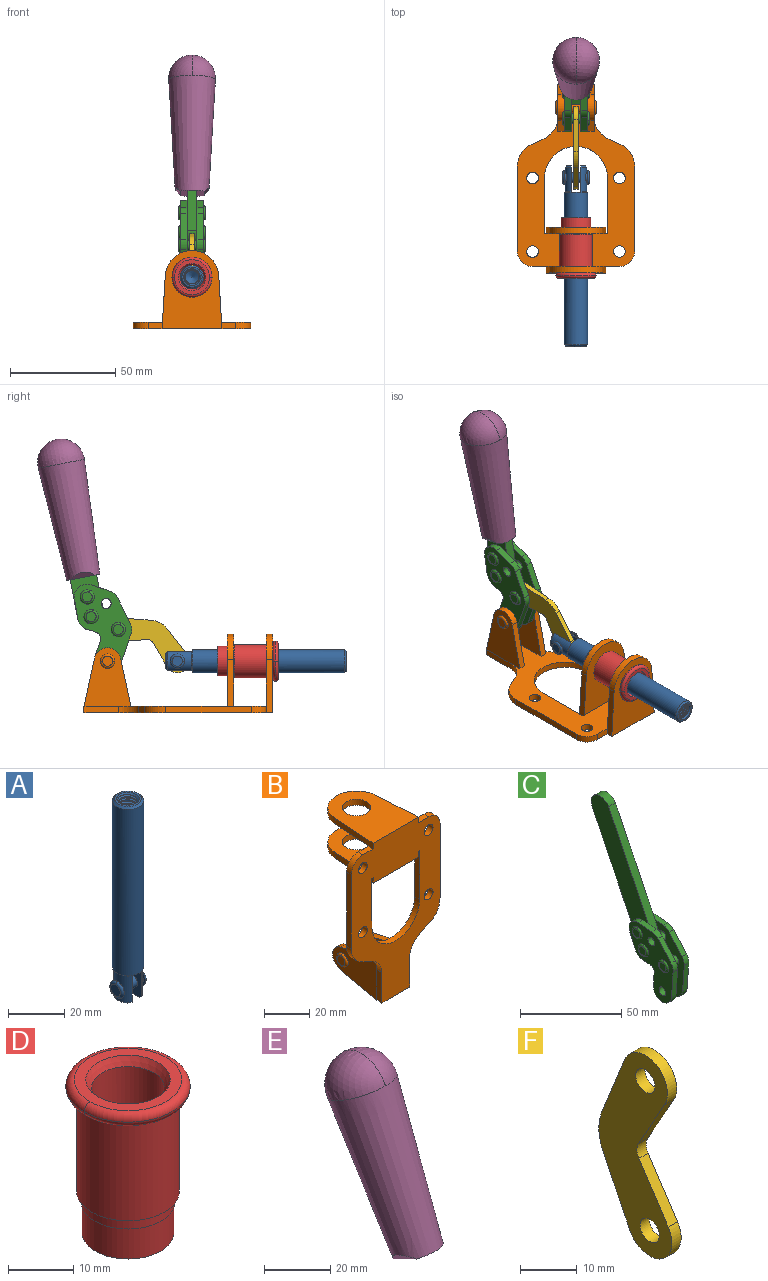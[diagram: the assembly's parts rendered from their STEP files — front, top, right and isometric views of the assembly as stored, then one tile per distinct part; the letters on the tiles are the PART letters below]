
ASSEMBLY  parts=6 mates=6
PART A: 48 faces, bbox 12.6x11.1x86.1 mm
  f0: torus R=2.41mm, axis (-1,0,0), area 15mm2, adj f30,f32,f34
  f1: torus R=2.41mm, axis (-1,0,0), area 15mm2, adj f29,f31,f33
  f2: cylinder r=5.54mm len=72.39mm, axis (0,0,1), area 2518.5mm2, adj f3,f4,f42,f43
  f3: cone r=5.54mm half-angle=45deg, axis (0,0,1), area 7.6mm2, adj f2,f5,f41
  f4: cone r=5.54mm half-angle=45deg, axis (0,0,-1), area 34.9mm2, adj f2,f39
  f5: cylinder r=5.08mm len=11.48mm, axis (0,0,1), area 108.3mm2, adj f3,f7,f8,f41
  f6: cylinder r=2.41mm len=4.83mm, axis (-1,0,0), area 71.2mm2, adj f40,f41
  f7: cylinder r=2.41mm len=4.83mm, axis (-1,0,0), area 7.6mm2, adj f5,f34
  f8: cone r=5.08mm half-angle=45deg, axis (0,0,1), area 10.6mm2, adj f5,f37,f41
  f9: cone r=3.98mm half-angle=45deg, axis (0,0,1), area 17.6mm2, adj f27,f39,f45,f46,f47
  f10: cylinder r=2.41mm len=4.83mm, axis (-1,0,0), area 7.6mm2, adj f33,f38
  f11: cylinder r=3.2mm len=6.4mm, axis (0,0,1), area 78.4mm2, adj f12,f28,f44,f45,f47
  f12: cylinder r=3.2mm len=6.4mm, axis (0,0,1), area 10.5mm2, adj f11,f13,f45,f47
  f13: cylinder r=3.2mm len=6.4mm, axis (0,0,1), area 10.5mm2, adj f12,f14,f45,f47
  f14: cylinder r=3.2mm len=6.4mm, axis (0,0,1), area 10.5mm2, adj f13,f15,f45,f47
  f15: cylinder r=3.2mm len=6.4mm, axis (0,0,1), area 10.5mm2, adj f14,f16,f45,f47
  f16: cylinder r=3.2mm len=6.4mm, axis (0,0,1), area 10.5mm2, adj f15,f17,f45,f47
  f17: cylinder r=3.2mm len=6.4mm, axis (0,0,1), area 10.5mm2, adj f16,f18,f45,f47
  f18: cylinder r=3.2mm len=6.4mm, axis (0,0,1), area 10.5mm2, adj f17,f19,f45,f47
  f19: cylinder r=3.2mm len=6.4mm, axis (0,0,1), area 10.5mm2, adj f18,f20,f45,f47
  f20: cylinder r=3.2mm len=6.4mm, axis (0,0,1), area 10.5mm2, adj f19,f21,f45,f47
  f21: cylinder r=3.2mm len=6.4mm, axis (0,0,1), area 10.5mm2, adj f20,f22,f45,f47
  f22: cylinder r=3.2mm len=6.4mm, axis (0,0,1), area 10.5mm2, adj f21,f23,f45,f47
  f23: cylinder r=3.2mm len=6.4mm, axis (0,0,1), area 10.5mm2, adj f22,f24,f45,f47
  f24: cylinder r=3.2mm len=6.4mm, axis (0,0,1), area 10.5mm2, adj f23,f25,f45,f47
  f25: cylinder r=3.2mm len=6.4mm, axis (0,0,1), area 10.5mm2, adj f24,f26,f45,f47
  f26: cylinder r=3.2mm len=6.4mm, axis (0,0,1), area 10.5mm2, adj f25,f27,f45,f47
  f27: cylinder r=3.2mm len=6.4mm, axis (0,0,1), area 7.4mm2, adj f9,f26,f45,f47
  f28: cone r=3.2mm half-angle=60deg, axis (0,0,1), area 37.2mm2, adj f11
  f29: plane 4.83x4.83mm, normal (-1,0,0), area 18.3mm2, adj f1,f31
  f30: plane 4.83x4.83mm, normal (1,0,0), area 18.3mm2, adj f0,f32
  f31: torus R=2.41mm, axis (-1,0,0), area 15mm2, adj f1,f29,f33
  f32: torus R=2.41mm, axis (-1,0,0), area 15mm2, adj f0,f30,f34
  f33: plane 6.83x6.83mm, normal (1,0,0), area 18.3mm2, adj f1,f10,f31
  f34: plane 6.83x6.83mm, normal (-1,0,0), area 18.3mm2, adj f0,f7,f32
  f35: cone r=5.08mm half-angle=45deg, axis (0,0,1), area 10.6mm2, adj f36,f38,f40
  f36: plane 7.25x1.97mm, normal (0,0,-1), area 10mm2, adj f35,f40
  f37: plane 7.25x1.97mm, normal (0,0,-1), area 10mm2, adj f8,f41
  f38: cylinder r=5.08mm len=11.48mm, axis (0,0,1), area 108.3mm2, adj f10,f35,f40,f42
  f39: plane 9.55x9.55mm, normal (0,0,1), area 22mm2, adj f4,f9
  f40: plane 12.76x10.09mm, normal (1,0,0), area 95.7mm2, adj f6,f35,f36,f38,f42,f43
  f41: plane 12.76x10.09mm, normal (-1,0,0), area 95.7mm2, adj f3,f5,f6,f8,f37,f43
  f42: cone r=5.54mm half-angle=45deg, axis (0,0,1), area 7.6mm2, adj f2,f38,f40
  f43: plane 11.07x4.7mm, normal (0,0,-1), area 50.4mm2, adj f2,f40,f41
  f44: plane 0.89x0.62mm, normal (-1,0,0), area 0.3mm2, adj f11,f45,f46,f47
  f45: bspline ~24.8x7.63mm, area 266.6mm2, adj f9,f11,f12,f13,f14,f15,f16,f17
  f46: bspline ~24.87x7.63mm, area 73.6mm2, adj f9,f44,f45,f47
  f47: bspline ~24.98x7.63mm, area 272.5mm2, adj f9,f11,f12,f13,f14,f15,f16,f17
PART B: 55 faces, bbox 55.7x37.4x89.8 mm
  f0: torus R=2.41mm, axis (-1,0,0), area 15mm2, adj f11,f15,f25
  f1: torus R=2.41mm, axis (-1,0,0), area 15mm2, adj f10,f12,f22
  f2: cylinder r=2.78mm len=5.56mm, axis (0,-1,0), area 54.2mm2, adj f30,f54
  f3: cylinder r=14.99mm len=29.97mm, axis (0,-1,0), area 145.9mm2, adj f30,f49,f53,f54
  f4: cylinder r=2.78mm len=5.56mm, axis (0,-1,0), area 54.2mm2, adj f30,f54
  f5: cylinder r=2.78mm len=5.56mm, axis (0,-1,0), area 54.2mm2, adj f30,f54
  f6: cylinder r=2.78mm len=5.56mm, axis (0,-1,0), area 54.2mm2, adj f30,f54
  f7: cylinder r=6.35mm len=12.7mm, axis (0,0,1), area 123.6mm2, adj f27,f51
  f8: cylinder r=6.35mm len=12.7mm, axis (0,0,-1), area 124.7mm2, adj f21,f35
  f9: cylinder r=2.41mm len=11.18mm, axis (-1,0,0), area 169.4mm2, adj f16,f19
  f10: plane 4.83x4.83mm, normal (1,0,0), area 18.3mm2, adj f1,f12
  f11: plane 4.83x4.83mm, normal (-1,0,0), area 18.3mm2, adj f0,f15
  f12: torus R=2.41mm, axis (-1,0,0), area 15mm2, adj f1,f10,f22
  f13: cylinder r=6.35mm len=12.41mm, axis (1,0,0), area 53.4mm2, adj f18,f19,f22,f23
  f14: cylinder r=6.35mm len=12.41mm, axis (-1,0,0), area 53.4mm2, adj f16,f17,f24,f25
  f15: torus R=2.41mm, axis (-1,0,0), area 15mm2, adj f0,f11,f25
  f16: plane 27.86x22.35mm, normal (1,0,0), area 425.4mm2, adj f9,f14,f17,f24,f30
  f17: plane 22.86x4.97mm, normal (0,0.21,0.98), area 72.5mm2, adj f14,f16,f25,f30
  f18: plane 22.86x4.97mm, normal (0,0.21,0.98), area 72.5mm2, adj f13,f19,f22,f30
  f19: plane 27.86x22.35mm, normal (-1,0,0), area 425.4mm2, adj f9,f13,f18,f23,f30
  f20: cylinder r=12.7mm len=25.35mm, axis (0,0,-1), area 119.8mm2, adj f21,f34,f35,f36
  f21: plane 34.21x28.07mm, normal (0,0,-1), area 702.4mm2, adj f8,f20,f30,f34,f36
  f22: plane 27.96x22.45mm, normal (1,0,0), area 407.2mm2, adj f1,f12,f13,f18,f23,f30,f42,f43
  f23: plane 22.86x4.97mm, normal (0,0.21,-0.98), area 72.5mm2, adj f13,f19,f22,f44
  f24: plane 22.86x4.97mm, normal (0,0.21,-0.98), area 72.5mm2, adj f14,f16,f25,f44
  f25: plane 27.86x22.35mm, normal (-1,0,0), area 407.1mm2, adj f0,f14,f15,f17,f24,f30,f45,f46
  f26: plane 3.1x0.95mm, normal (0,0,-1), area 2.7mm2, adj f30,f49,f50,f54
  f27: plane 34.21x28.07mm, normal (0,0,1), area 702.4mm2, adj f7,f28,f30,f50,f52
  f28: cylinder r=12.7mm len=25.35mm, axis (0,0,1), area 118.8mm2, adj f27,f50,f51,f52
  f29: plane 3.1x0.95mm, normal (0,0,-1), area 2.7mm2, adj f30,f52,f53,f54
  f30: plane 86.54x55.63mm, normal (0,1,0), area 2362.9mm2, adj f2,f3,f4,f5,f6,f16,f17,f18
  f31: plane 40.56x3.1mm, normal (-1,0,0), area 125.7mm2, adj f30,f32,f48,f54
  f32: cylinder r=7.11mm len=7.11mm, axis (0,-1,0), area 34.6mm2, adj f30,f31,f33,f54
  f33: plane 6.67x3.1mm, normal (0,0,1), area 20.4mm2, adj f30,f32,f34,f54
  f34: plane 25.39x3.13mm, normal (-1,0.06,0), area 79.5mm2, adj f20,f21,f33,f35,f54
  f35: plane 37.31x28.45mm, normal (0,0,1), area 789.9mm2, adj f8,f20,f34,f36,f54
  f36: plane 25.39x3.13mm, normal (1,0.06,0), area 79.5mm2, adj f20,f21,f35,f37,f54
  f37: plane 6.67x3.1mm, normal (0,0,1), area 20.4mm2, adj f30,f36,f38,f54
  f38: cylinder r=7.11mm len=7.11mm, axis (0,-1,0), area 34.6mm2, adj f30,f37,f39,f54
  f39: plane 40.56x3.1mm, normal (1,0,0), area 125.7mm2, adj f30,f38,f40,f54
  f40: cylinder r=11.18mm len=10.16mm, axis (0,-1,0), area 39.5mm2, adj f30,f39,f41,f54
  f41: plane 6.09x3.1mm, normal (0.42,0,-0.91), area 20.8mm2, adj f30,f40,f42,f54
  f42: cylinder r=11.18mm len=9.41mm, axis (0,-1,0), area 37.2mm2, adj f22,f30,f41,f43,f54
  f43: plane 16.5x3.1mm, normal (1,0,0), area 51.1mm2, adj f22,f42,f44,f54
  f44: plane 17.37x3.1mm, normal (0,0,-1), area 53.8mm2, adj f23,f24,f30,f43,f45,f54
  f45: plane 16.5x3.1mm, normal (-1,0,0), area 51.1mm2, adj f25,f44,f46,f54
  f46: cylinder r=11.18mm len=9.41mm, axis (0,-1,0), area 37.2mm2, adj f25,f30,f45,f47,f54
  f47: plane 6.09x3.1mm, normal (-0.42,0,-0.91), area 20.8mm2, adj f30,f46,f48,f54
  f48: cylinder r=11.18mm len=10.16mm, axis (0,-1,0), area 39.5mm2, adj f30,f31,f47,f54
  f49: plane 26.54x3.1mm, normal (-1,0,0), area 82.3mm2, adj f3,f26,f30,f54
  f50: plane 25.39x3.1mm, normal (1,0.06,0), area 78.8mm2, adj f26,f27,f28,f51,f54
  f51: plane 37.31x28.45mm, normal (0,0,-1), area 789.9mm2, adj f7,f28,f50,f52,f54
  f52: plane 25.39x3.1mm, normal (-1,0.06,0), area 78.8mm2, adj f27,f28,f29,f51,f54
  f53: plane 26.54x3.1mm, normal (1,0,0), area 82.3mm2, adj f3,f29,f30,f54
  f54: plane 89.66x55.63mm, normal (0,-1,0), area 2678.5mm2, adj f2,f3,f4,f5,f6,f26,f29,f31
PART C: 59 faces, bbox 12.9x60.2x99.6 mm
  f0: torus R=2.39mm, axis (-1,0,0), area 14.9mm2, adj f20,f43,f51
  f1: torus R=2.39mm, axis (-1,0,0), area 14.9mm2, adj f19,f42,f51
  f2: torus R=2.39mm, axis (-1,0,0), area 14.9mm2, adj f18,f35,f51
  f3: torus R=2.39mm, axis (-1,0,0), area 14.9mm2, adj f14,f17,f23
  f4: torus R=2.39mm, axis (-1,0,0), area 14.9mm2, adj f13,f16,f23
  f5: torus R=2.39mm, axis (-1,0,0), area 14.9mm2, adj f12,f15,f23
  f6: cylinder r=2.39mm len=4.78mm, axis (1,0,0), area 46.5mm2, adj f48,f50,f51
  f7: cylinder r=2.39mm len=4.78mm, axis (1,0,0), area 46.5mm2, adj f50,f51
  f8: cylinder r=6.35mm len=12.68mm, axis (1,0,0), area 61.8mm2, adj f38,f39,f50,f51
  f9: cylinder r=2.39mm len=4.78mm, axis (-1,0,0), area 70.5mm2, adj f46,f50
  f10: cylinder r=2.39mm len=4.78mm, axis (-1,0,0), area 46.5mm2, adj f23,f45,f46
  f11: cylinder r=2.39mm len=4.78mm, axis (-1,0,0), area 46.5mm2, adj f23,f46
  f12: plane 4.78x4.78mm, normal (1,0,0), area 17.9mm2, adj f5,f15
  f13: plane 4.78x4.78mm, normal (1,0,0), area 17.9mm2, adj f4,f16
  f14: plane 4.78x4.78mm, normal (1,0,0), area 17.9mm2, adj f3,f17
  f15: torus R=2.39mm, axis (-1,0,0), area 14.9mm2, adj f5,f12,f23
  f16: torus R=2.39mm, axis (-1,0,0), area 14.9mm2, adj f4,f13,f23
  f17: torus R=2.39mm, axis (-1,0,0), area 14.9mm2, adj f3,f14,f23
  f18: plane 4.78x4.78mm, normal (-1,0,0), area 17.9mm2, adj f2,f35
  f19: plane 4.78x4.78mm, normal (-1,0,0), area 17.9mm2, adj f1,f42
  f20: plane 4.78x4.78mm, normal (-1,0,0), area 17.9mm2, adj f0,f43
  f21: plane 2.26x0.2mm, normal (1,0,0), area 0.2mm2, adj f31,f44
  f22: plane 2.26x0.2mm, normal (-1,0,0), area 0.2mm2, adj f41,f44
  f23: plane 39.37x30.77mm, normal (1,0,0), area 565.5mm2, adj f3,f4,f5,f10,f11,f15,f16,f17
  f24: cylinder r=6.1mm len=4.15mm, axis (-1,0,0), area 14.7mm2, adj f23,f25,f32,f46
  f25: plane 10.25x9.01mm, normal (0,-0.75,0.66), area 42.3mm2, adj f23,f24,f26,f46
  f26: cylinder r=6.35mm len=4.64mm, axis (-1,0,0), area 15.6mm2, adj f23,f25,f27,f46
  f27: plane 15.84x3.1mm, normal (0,-1,-0.07), area 49.2mm2, adj f23,f26,f28,f46
  f28: cylinder r=6.35mm len=12.68mm, axis (-1,0,0), area 61.8mm2, adj f23,f27,f29,f46
  f29: plane 8.11x3.1mm, normal (0,1,0.07), area 25.2mm2, adj f23,f28,f30,f46
  f30: cylinder r=3.05mm len=3.25mm, axis (-1,0,0), area 14.8mm2, adj f23,f29,f31,f46
  f31: plane 5.99x3.1mm, normal (0,0.07,-1), area 18.6mm2, adj f21,f23,f30,f44,f46
  f32: plane 9.5x3.1mm, normal (0,-0.07,1), area 29.5mm2, adj f23,f24,f33,f46,f47
  f33: cylinder r=6.1mm len=8.63mm, axis (-1,0,0), area 39.1mm2, adj f23,f32,f34,f47
  f34: plane 8.65x3.96mm, normal (0,0.91,-0.42), area 29.5mm2, adj f23,f33,f44,f47
  f35: torus R=2.39mm, axis (-1,0,0), area 14.9mm2, adj f2,f18,f51
  f36: plane 10.25x9.01mm, normal (0,-0.75,0.66), area 42.3mm2, adj f37,f49,f50,f51
  f37: cylinder r=6.35mm len=4.64mm, axis (1,0,0), area 15.6mm2, adj f36,f38,f50,f51
  f38: plane 15.84x3.1mm, normal (0,-1,-0.07), area 49.2mm2, adj f8,f37,f50,f51
  f39: plane 8.11x3.1mm, normal (0,1,0.07), area 25.2mm2, adj f8,f40,f50,f51
  f40: cylinder r=3.05mm len=3.25mm, axis (1,0,0), area 14.8mm2, adj f39,f41,f50,f51
  f41: plane 5.99x3.1mm, normal (0,0.07,-1), area 18.6mm2, adj f22,f40,f44,f50,f51
  f42: torus R=2.39mm, axis (-1,0,0), area 14.9mm2, adj f1,f19,f51
  f43: torus R=2.39mm, axis (-1,0,0), area 14.9mm2, adj f0,f20,f51
  f44: cylinder r=6.35mm len=12.12mm, axis (-1,0,0), area 128.9mm2, adj f21,f22,f23,f31,f34,f41,f46,f47
  f45: plane 2.65x1.35mm, normal (1,0,0), area 1mm2, adj f10,f55
  f46: plane 39.08x20.42mm, normal (-1,0,0), area 412.5mm2, adj f9,f10,f11,f24,f25,f26,f27,f28
  f47: plane 77.62x39.82mm, normal (1,0,0), area 850mm2, adj f32,f33,f34,f44,f53,f54,f55
  f48: plane 2.65x1.35mm, normal (-1,0,0), area 1mm2, adj f6,f55
  f49: cylinder r=6.1mm len=4.15mm, axis (1,0,0), area 14.7mm2, adj f36,f50,f51,f56
  f50: plane 39.08x20.42mm, normal (1,0,0), area 412.5mm2, adj f6,f7,f8,f9,f36,f37,f38,f39
  f51: plane 39.37x30.77mm, normal (-1,0,0), area 565.5mm2, adj f0,f1,f2,f6,f7,f8,f35,f36
  f52: plane 8.65x3.96mm, normal (0,0.91,-0.42), area 29.5mm2, adj f44,f51,f57,f58
  f53: plane 68.49x33.4mm, normal (0,0.9,-0.44), area 358.1mm2, adj f44,f47,f54,f58
  f54: cylinder r=6.35mm len=12.06mm, axis (1,0,0), area 93.7mm2, adj f47,f53,f55,f58
  f55: plane 68.49x33.4mm, normal (0,-0.9,0.44), area 358.1mm2, adj f44,f45,f46,f47,f48,f50,f54,f58
  f56: plane 9.5x3.1mm, normal (0,-0.07,1), area 29.5mm2, adj f49,f50,f51,f57,f58
  f57: cylinder r=6.1mm len=8.63mm, axis (1,0,0), area 39.1mm2, adj f51,f52,f56,f58
  f58: plane 77.62x39.82mm, normal (-1,0,0), area 850mm2, adj f44,f52,f53,f54,f55,f56,f57
PART D: 15 faces, bbox 20.6x20.6x28.7 mm
  f0: torus R=8.26mm, axis (0,0,1), area 56.8mm2, adj f1,f10,f12
  f1: torus R=8.26mm, axis (0,0,1), area 56.8mm2, adj f0,f6,f13
  f2: cylinder r=5.59mm len=25.91mm, axis (0,0,1), area 909.6mm2, adj f3,f4
  f3: cone r=6.86mm half-angle=45deg, axis (0,0,-1), area 70.2mm2, adj f2,f14
  f4: cone r=6.47mm half-angle=30deg, axis (0,0,1), area 66.7mm2, adj f2,f13
  f5: cylinder r=7.04mm len=14.07mm, axis (0,0,1), area 252.6mm2, adj f11,f14
  f6: torus R=8.26mm, axis (0,0,1), area 56.8mm2, adj f1,f12,f13
  f7: cylinder r=7.16mm len=14.33mm, axis (0,0,1), area 91.5mm2, adj f9,f11
  f8: cylinder r=7.86mm len=18.42mm, axis (0,0,1), area 909.6mm2, adj f9,f10
  f9: plane 15.72x15.72mm, normal (0,0,-1), area 33mm2, adj f7,f8
  f10: plane 16.51x16.51mm, normal (0,0,-1), area 19.9mm2, adj f0,f8,f12
  f11: plane 14.33x14.33mm, normal (0,0,-1), area 5.7mm2, adj f5,f7
  f12: torus R=8.26mm, axis (0,0,1), area 56.8mm2, adj f0,f6,f10
  f13: plane 16.51x16.51mm, normal (0,0,1), area 82.7mm2, adj f1,f4,f6
  f14: plane 14.07x14.07mm, normal (0,0,-1), area 7.8mm2, adj f3,f5
PART E: 11 faces, bbox 22.3x42.6x64.5 mm
  f0: sphere r=11.13mm, area 411.4mm2, adj f1,f8
  f1: cone r=11.11mm half-angle=3.3deg, axis (0,0.44,0.9), area 3251.8mm2, adj f0,f7,f8,f9,f10
  f2: cylinder r=6.16mm len=11.7mm, axis (1,0,0), area 89.5mm2, adj f3,f4,f5,f6
  f3: plane 60.23x36.75mm, normal (-1,0,0), area 763.6mm2, adj f2,f4,f6,f10
  f4: plane 51.37x25.05mm, normal (0,0.9,-0.44), area 264.2mm2, adj f2,f3,f5,f10
  f5: plane 60.23x36.75mm, normal (1,0,0), area 763.6mm2, adj f2,f4,f6,f10
  f6: plane 51.37x25.05mm, normal (0,-0.9,0.44), area 264.2mm2, adj f2,f3,f5,f10
  f7: plane 9.95x5.95mm, normal (0.71,-0.31,-0.64), area 25.8mm2, adj f1,f10
  f8: sphere r=11.13mm, area 411.4mm2, adj f0,f1
  f9: plane 9.95x5.95mm, normal (-0.71,-0.31,-0.64), area 25.8mm2, adj f1,f10
  f10: plane 14.27x11.38mm, normal (0,-0.44,-0.9), area 106.7mm2, adj f1,f3,f4,f5,f6,f7,f9
PART F: 12 faces, bbox 2.3x18.2x42.8 mm
  f0: cylinder r=2.4mm len=4.8mm, axis (1,0,0), area 34.9mm2, adj f4,f11
  f1: cylinder r=10.41mm len=8.47mm, axis (1,0,0), area 20.2mm2, adj f4,f9,f10,f11
  f2: cylinder r=3.05mm len=3.16mm, axis (1,0,0), area 7.7mm2, adj f4,f6,f7,f11
  f3: cylinder r=2.4mm len=4.8mm, axis (1,0,0), area 34.9mm2, adj f4,f11
  f4: plane 42.81x18.23mm, normal (-1,0,0), area 414.1mm2, adj f0,f1,f2,f3,f5,f6,f7,f8
  f5: cylinder r=5.54mm len=10.67mm, axis (1,0,0), area 41.8mm2, adj f4,f6,f10,f11
  f6: plane 11.66x6.53mm, normal (0,-0.87,-0.49), area 30.9mm2, adj f2,f4,f5,f11
  f7: plane 11.17x7.33mm, normal (0,-0.84,0.55), area 30.9mm2, adj f2,f4,f8,f11
  f8: cylinder r=5.54mm len=10.51mm, axis (1,0,0), area 41.8mm2, adj f4,f7,f9,f11
  f9: plane 13.67x6.67mm, normal (0,0.9,-0.44), area 35.1mm2, adj f1,f4,f8,f11
  f10: plane 14.1x5.7mm, normal (0,0.93,0.37), area 35.1mm2, adj f1,f4,f5,f11
  f11: plane 42.81x18.23mm, normal (1,0,0), area 414.1mm2, adj f0,f1,f2,f3,f5,f6,f7,f8
PLACE A rot(axis=(1,0,0),90deg) t=(0,23.56,0)mm
PLACE B rot(axis=(1,0,0),90deg) t=(0,9.14,0)mm fixed
PLACE C rot(axis=(1,0,0),15deg) t=(0,9.15,49.24)mm
PLACE D rot(axis=(1,0,0),90deg) t=(0,9.14,0)mm
PLACE E rot(axis=(1,0,0),15deg) t=(0.04,9.15,49.24)mm
PLACE F rot(axis=(1,0,0),120.2deg) t=(0,33.84,11.13)mm
MATE revolute F.f3 <-> C.f4  axis (1,0,0) through (0,36.06,39.62)mm
MATE fastened E.f2 <-> C.f54  axis (-1,0,0) through (2.35,63.6,120.54)mm
MATE revolute C.f7 <-> B.f0  axis (-1,0,0) through (0,41.23,24.61)mm
MATE slider A.f2 <-> B.f7  axis (0,-1,0) through (0,-35.22,24.61)mm
MATE fastened D.f2 <-> B.f7  axis (0,1,0) through (0,-37.25,24.61)mm
MATE revolute F.f5 <-> A.f6  axis (1,0,0) through (0,8.09,24.61)mm
